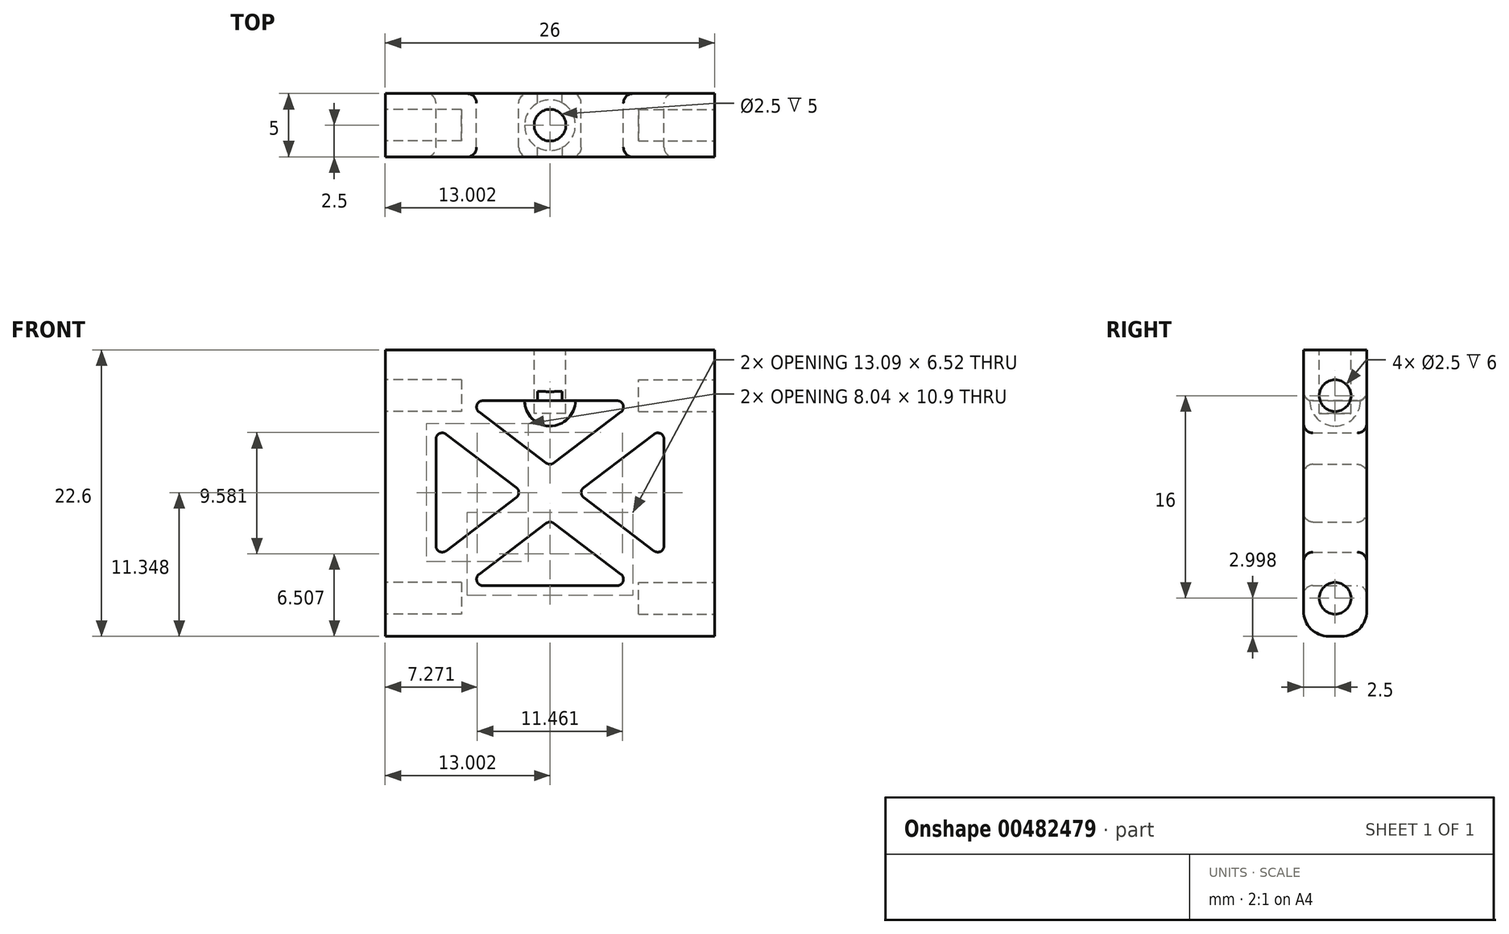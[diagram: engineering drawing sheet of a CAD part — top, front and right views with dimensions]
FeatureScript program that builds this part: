
annotation { "Feature Type Name" : "Feature", "Feature Type Description" : "" }
export const myFeature = defineFeature(function(context is Context, id is Id, definition is map)
    precondition{}
    {
        {
            var Q0;
            Q0=qCreatedBy(makeId("Front.planeOp"),FACE);
            var sketch = newSketch(context, id + "F0", { "sketchPlane" : qUnion([Q0])});
            skLineSegment(sketch, "E0.bottom", {"start": v(-26.66, 25.94) * mm, "end": v(-52.66, 25.94) * mm});
            skLineSegment(sketch, "E0.top", {"start": v(-26.66, 48.54) * mm, "end": v(-52.66, 48.54) * mm});
            skLineSegment(sketch, "E0.left", {"start": v(-26.66, 25.94) * mm, "end": v(-26.66, 48.54) * mm});
            skLineSegment(sketch, "E0.right", {"start": v(-52.66, 25.94) * mm, "end": v(-52.66, 48.54) * mm});
            skPoint(sketch, "E0.middle", {"position": v(-39.66, 37.24) * mm});
            skPoint(sketch, "E1.endSnap0", {"position": v(-52.66, 37.24) * mm});
            skLineSegment(sketch, "E2.0", {"start": v(-34.36, 44.54) * mm, "end": v(-44.95, 44.54) * mm});
            skLineSegment(sketch, "E2.1", {"start": v(-30.66, 33.08) * mm, "end": v(-30.66, 41.5) * mm});
            skLineSegment(sketch, "E2.2", {"start": v(-34.36, 29.94) * mm, "end": v(-44.95, 29.94) * mm});
            skLineSegment(sketch, "E2.3", {"start": v(-48.66, 33.08) * mm, "end": v(-48.66, 41.5) * mm});
            skLineSegment(sketch, "E3", {"start": v(-47.86, 41.9) * mm, "end": v(-42.32, 37.69) * mm});
            skLineSegment(sketch, "E4.MirrorCS", {"start": v(-47.86, 32.68) * mm, "end": v(-42.32, 36.89) * mm});
            skLineSegment(sketch, "E5.MirrorCS", {"start": v(-31.46, 41.9) * mm, "end": v(-37, 37.69) * mm});
            skLineSegment(sketch, "E6.MirrorCS", {"start": v(-31.46, 32.68) * mm, "end": v(-37, 36.89) * mm});
            skLineSegment(sketch, "E7", {"start": v(-45.25, 43.64) * mm, "end": v(-39.96, 39.62) * mm});
            skLineSegment(sketch, "E8.MirrorCS", {"start": v(-34.06, 43.64) * mm, "end": v(-39.36, 39.62) * mm});
            skLineSegment(sketch, "E9.MirrorCS", {"start": v(-45.25, 30.84) * mm, "end": v(-39.96, 34.86) * mm});
            skLineSegment(sketch, "E10.MirrorCS", {"start": v(-34.06, 30.84) * mm, "end": v(-39.36, 34.86) * mm});
            skPoint(sketch, "E11.visualSharp", {"position": v(-48.66, 42.5) * mm});
            skArc(sketch, "E11.filletArc", {"start": v(-47.86, 41.9) * mm, "mid": v(-48.38, 41.94) * mm, "end": v(-48.66, 41.5) * mm});
            skPoint(sketch, "E12.visualSharp", {"position": v(-48.66, 32.07) * mm});
            skArc(sketch, "E12.filletArc", {"start": v(-48.66, 33.08) * mm, "mid": v(-48.38, 32.63) * mm, "end": v(-47.86, 32.68) * mm});
            skPoint(sketch, "E13.visualSharp", {"position": v(-46.44, 29.94) * mm});
            skArc(sketch, "E13.filletArc", {"start": v(-45.25, 30.84) * mm, "mid": v(-45.43, 30.28) * mm, "end": v(-44.95, 29.94) * mm});
            skPoint(sketch, "E14.visualSharp", {"position": v(-30.66, 32.07) * mm});
            skArc(sketch, "E14.filletArc", {"start": v(-31.46, 32.68) * mm, "mid": v(-30.94, 32.63) * mm, "end": v(-30.66, 33.08) * mm});
            skPoint(sketch, "E15.visualSharp", {"position": v(-30.66, 42.5) * mm});
            skArc(sketch, "E15.filletArc", {"start": v(-30.66, 41.5) * mm, "mid": v(-30.94, 41.94) * mm, "end": v(-31.46, 41.9) * mm});
            skPoint(sketch, "E16.visualSharp", {"position": v(-32.88, 29.94) * mm});
            skArc(sketch, "E16.filletArc", {"start": v(-34.36, 29.94) * mm, "mid": v(-33.9, 30.28) * mm, "end": v(-34.06, 30.84) * mm});
            skPoint(sketch, "E17.visualSharp", {"position": v(-32.88, 44.54) * mm});
            skArc(sketch, "E17.filletArc", {"start": v(-34.06, 43.64) * mm, "mid": v(-33.9, 44.2) * mm, "end": v(-34.36, 44.54) * mm});
            skPoint(sketch, "E18.visualSharp", {"position": v(-46.44, 44.54) * mm});
            skArc(sketch, "E18.filletArc", {"start": v(-44.95, 44.54) * mm, "mid": v(-45.43, 44.2) * mm, "end": v(-45.25, 43.64) * mm});
            skPoint(sketch, "E19.visualSharp", {"position": v(-39.66, 39.4) * mm});
            skArc(sketch, "E19.filletArc", {"start": v(-39.96, 39.62) * mm, "mid": v(-39.66, 39.52) * mm, "end": v(-39.36, 39.62) * mm});
            skPoint(sketch, "E20.visualSharp", {"position": v(-37.52, 37.29) * mm});
            skArc(sketch, "E20.filletArc", {"start": v(-37, 37.69) * mm, "mid": v(-37.2, 37.29) * mm, "end": v(-37, 36.89) * mm});
            skPoint(sketch, "E21.visualSharp", {"position": v(-39.66, 35.09) * mm});
            skArc(sketch, "E21.filletArc", {"start": v(-39.36, 34.86) * mm, "mid": v(-39.66, 34.96) * mm, "end": v(-39.96, 34.86) * mm});
            skPoint(sketch, "E22.visualSharp", {"position": v(-41.8, 37.29) * mm});
            skArc(sketch, "E22.filletArc", {"start": v(-42.32, 36.89) * mm, "mid": v(-42.12, 37.29) * mm, "end": v(-42.32, 37.69) * mm});
            skSolve(sketch);
        }
        {
            var Q0;
            Q0 = qSketchRegion(id + "F0", true);
            extrude(context, id + "F1", {"entities" : qUnion([Q0]), "depth" : 5 * mm, "offsetDistance" : 25 * mm});
        }
        {
            var Q0;
            Q0=makeQuery(id+"F1.opExtrude","SWEPT_FACE",FACE,{"disambiguationData":[OSD([sQuery(id+"F0.wireOp",EDGE,"E0.left")])]});
            var sketch = newSketch(context, id + "F2", { "sketchPlane" : qUnion([Q0])});
            skLineSegment(sketch, "E23", {"start": v(-2.5, 48.54) * mm, "end": v(-2.5, 25.94) * mm, "construction": true});
            skCircle(sketch, "E24", {"center": v(-2.5, 28.94) * mm, "radius": 1.25 * mm});
            skCircle(sketch, "E25", {"center": v(-2.5, 44.94) * mm, "radius": 1.25 * mm});
            skSolve(sketch);
        }
        {
            var Q0;
            Q0=makeQuery(id+"F1.opExtrude","SWEPT_FACE",FACE,{"disambiguationData":[OSD([sQuery(id+"F0.wireOp",EDGE,"E0.right")])]});
            var sketch = newSketch(context, id + "F3", { "sketchPlane" : qUnion([Q0])});
            skLineSegment(sketch, "E26", {"start": v(2.5, 48.44) * mm, "end": v(2.5, 25.94) * mm, "construction": true});
            skCircle(sketch, "E27", {"center": v(2.5, 28.94) * mm, "radius": 1.25 * mm});
            skCircle(sketch, "E28", {"center": v(2.5, 44.94) * mm, "radius": 1.25 * mm});
            skSolve(sketch);
        }
        {
            var Q0;
            Q0 = qSketchRegion(id + "F3", true);
            extrude(context, id + "F4", {"entities" : qUnion([Q0]), "operationType" : NewBodyOperationType.REMOVE, "oppositeDirection" : true, "depth" : 6 * mm, "offsetDistance" : 25 * mm});
        }
        {
            var Q0;
            Q0 = qSketchRegion(id + "F2", true);
            extrude(context, id + "F5", {"entities" : qUnion([Q0]), "operationType" : NewBodyOperationType.REMOVE, "oppositeDirection" : true, "depth" : 6 * mm, "offsetDistance" : 25 * mm});
        }
        {
            var Q0;
            Q0=makeQuery(id+"F1.opExtrude","SWEPT_FACE",FACE,{"disambiguationData":[OSD([sQuery(id+"F0.wireOp",EDGE,"E2.0")])]});
            var sketch = newSketch(context, id + "F6", { "sketchPlane" : qUnion([Q0])});
            skCircle(sketch, "E29", {"center": v(-39.66, 2.5) * mm, "radius": 2 * mm});
            skSolve(sketch);
        }
        {
            var Q0;
            Q0=makeQuery(id+"F6.imprint","IMPRINT",FACE,{"disambiguationData":[TD([[makeQuery(id+"F6.imprint","IMPRINT",EDGE,{"derivedFrom":sQuery(id+"F6.wireOp",EDGE,"E29")}),1.0]])]});
            extrude(context, id + "F7", {"entities" : qUnion([Q0]), "operationType" : NewBodyOperationType.ADD, "depth" : 2 * mm, "offsetDistance" : 25 * mm});
        }
        {
            var Q0;
            Q0=makeQuery(id+"F1.opExtrude","SWEPT_FACE",FACE,{"disambiguationData":[OSD([sQuery(id+"F0.wireOp",EDGE,"E0.top")])]});
            var sketch = newSketch(context, id + "F8", { "sketchPlane" : qUnion([Q0])});
            skCircle(sketch, "E30", {"center": v(-39.66, -2.5) * mm, "radius": 1.25 * mm});
            skSolve(sketch);
        }
        {
            var Q0;
            Q0=makeQuery(id+"F8.imprint","IMPRINT",FACE,{"disambiguationData":[TD([[makeQuery(id+"F8.imprint","IMPRINT",EDGE,{"derivedFrom":sQuery(id+"F8.wireOp",EDGE,"E30")}),1.0]])]});
            extrude(context, id + "F9", {"entities" : qUnion([Q0]), "operationType" : NewBodyOperationType.REMOVE, "oppositeDirection" : true, "depth" : 5 * mm, "offsetDistance" : 25 * mm});
        }
        {
            var Q0;
            Q0=makeQuery(id+"F7.opExtrude","CAP_EDGE",EDGE,{"disambiguationData":[OSD([sQuery(id+"F6.wireOp",EDGE,"E29")])],"isStart":false});
            fillet(context, id + "F10", {"entities" : qUnion([Q0]), "radius" : 2 * mm, "tangentPropagation" : true, "allowEdgeOverflow" : false});
        }
        {
            var Q0;
            Q0=makeQuery(id+"F1.opExtrude","CAP_EDGE",EDGE,{"disambiguationData":[OSD([sQuery(id+"F0.wireOp",EDGE,"E2.0")])],"isStart":true});
            var Q1;
            Q1=makeQuery(id+"F1.opExtrude","CAP_EDGE",EDGE,{"disambiguationData":[OSD([sQuery(id+"F0.wireOp",EDGE,"E6.MirrorCS")])],"isStart":true});
            var Q2;
            Q2=makeQuery(id+"F1.opExtrude","CAP_EDGE",EDGE,{"disambiguationData":[OSD([sQuery(id+"F0.wireOp",EDGE,"E2.2")])],"isStart":true});
            var Q3;
            Q3=makeQuery(id+"F1.opExtrude","CAP_EDGE",EDGE,{"disambiguationData":[OSD([sQuery(id+"F0.wireOp",EDGE,"E2.3")])],"isStart":true});
            var Q4;
            Q4=makeQuery(id+"F1.opExtrude","CAP_EDGE",EDGE,{"disambiguationData":[OSD([sQuery(id+"F0.wireOp",EDGE,"E2.2")])],"isStart":false});
            var Q5;
            Q5=makeQuery(id+"F1.opExtrude","CAP_EDGE",EDGE,{"disambiguationData":[OSD([sQuery(id+"F0.wireOp",EDGE,"E2.1")])],"isStart":false});
            var Q6;
            Q6=makeQuery(id+"F1.opExtrude","CAP_EDGE",EDGE,{"disambiguationData":[OSD([sQuery(id+"F0.wireOp",EDGE,"E4.MirrorCS")])],"isStart":false});
            var Q7;
            Q7=makeQuery(id+"F1.opExtrude","CAP_EDGE",EDGE,{"disambiguationData":[OSD([sQuery(id+"F0.wireOp",EDGE,"E8.MirrorCS")])],"isStart":false});
            fillet(context, id + "F11", {"entities" : qUnion([Q0, Q1, Q2, Q3, Q4, Q5, Q6, Q7]), "radius" : .75 * mm, "tangentPropagation" : true, "allowEdgeOverflow" : false});
        }
        {
            var Q0;
            Q0=makeQuery(id+"F1.opExtrude","CAP_EDGE",EDGE,{"disambiguationData":[OSD([sQuery(id+"F0.wireOp",EDGE,"E0.bottom")])],"isStart":true});
            fillet(context, id + "F12", {"entities" : qUnion([Q0]), "radius" : 2 * mm, "tangentPropagation" : true, "allowEdgeOverflow" : false});
        }
        {
            var Q0;
            Q0=makeQuery(id+"F1.opExtrude","CAP_EDGE",EDGE,{"disambiguationData":[OSD([sQuery(id+"F0.wireOp",EDGE,"E0.bottom")])],"isStart":false});
            fillet(context, id + "F13", {"entities" : qUnion([Q0]), "radius" : 2 * mm, "tangentPropagation" : true, "allowEdgeOverflow" : false});
        }
    });
